# Revit family: DP 5EN
name_source: partatom
category: Dispositivi di comunicazione
units: mm (PartAtom-declared; Revit-internal decimal feet)

## family parameters
Condiviso = Sì
Host = Superficie
Mantenere orientamento annotazione = No
Numero OmniClass = 23.85.10.11.11.21
Punto di calcolo locali = No
Quota connettore circolare = Usa diametro
Taglio con vuoti quando caricato = No
Tipo di parte = Normale
Titolo OmniClass = Speakers

## types (1)
- DP 5EN
    CE marking = Yes
    CPR number = 0068-CPR-058/2014
    Cabinet/Case Material = ABS
    Color = White - RAL 9016
    Constant Voltage Transformer = 100 V
    Data sheet = https://www.rcf.it
    Depth = 261 mm / 10.28 inches
    Descrizione = DP 5EN is a 20 W weatherproof sound projector in compliance with EN 54-24 regulations.
It is suitable for all those installations where high intelligibility for alarm messages broadcasting and great sound reproduction quality are required; moreover, thanks to its IP 65 protection grade, it can be installed both indoor and outdoor.
A modern and endearing design makes it the perfect product for environments where projectors are intended also as architectural elements and contribute to improve global aesthetics.
    EN54-24 certified = Yes
    Frequency Response (-10dB) = 80 Hz ÷ 20000 Hz
    Grille = RCF- Steel
    Height = 183 mm / 7.2 inches
    Horizontal coverage angle = 210°
    IP protection grade = IP 65
    Input connectors = Ceramic screw terminals
    Max SPL @ 1m = 101 dB
    Max SPL @ 4m = 89 dB
    Modello = DP 5EN
    Output connectors = Ceramic screw terminals
    Part Numbers = 13133076
    Peak Power Handling = 80 W PEAK
    Power Handling = 20 W RMS
    Power selection 1 (100 V) = 20 W - 500 ohm
    Power selection 2 (100 V) = 10 W - 1000 ohm
    Power selection 3 (100 V) = 5 W - 2000 ohm
    Power selection 4 (100 V) = 2.5 W - 4000 ohm
    Produttore = RCF S.p.A.
Via Raffaello Sanzio, 13 
-
42124 Reggio Emilia Italy
    Prospetto di default = 1219 mm
    Protections = Thermal fuse
    Recommended Amplifier = 40 W
    System Sensitivity = 88 dB
    System Sensitivity 1W @ 4m = 76 dB
    URL = http://www.rcf.it
    Vertical coverage angle = 210°
    Weight = 2.61 kg / 5.75 lbs
    Width = 176 mm / 6.93 inches
